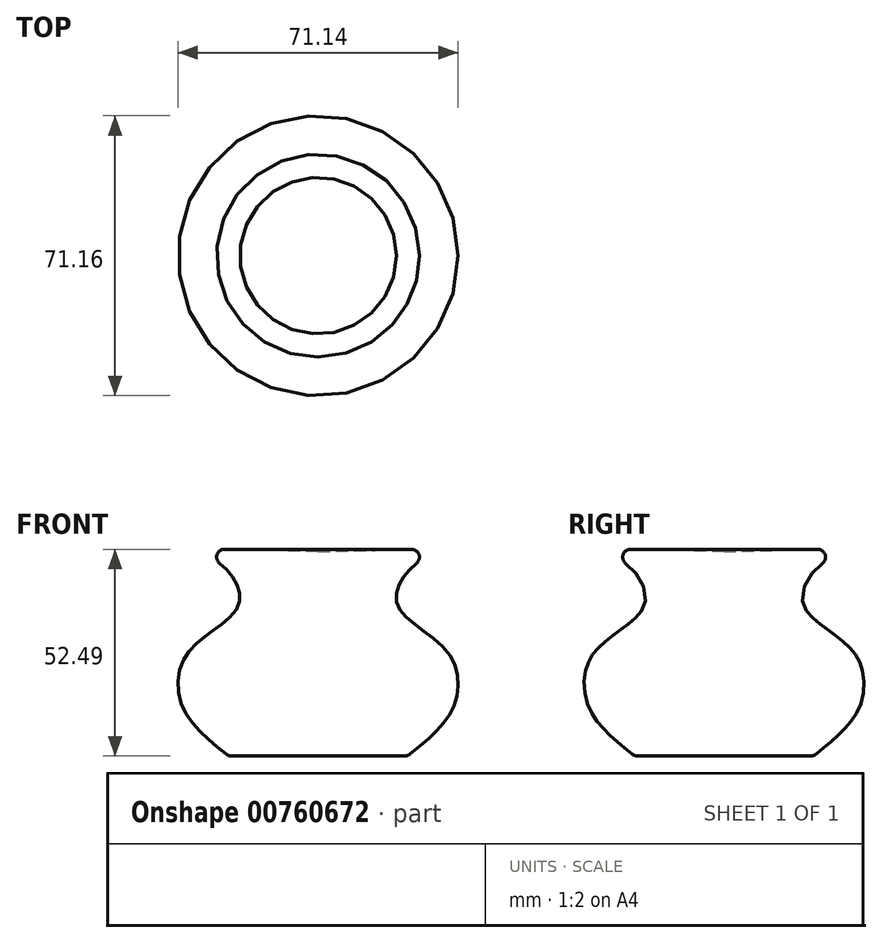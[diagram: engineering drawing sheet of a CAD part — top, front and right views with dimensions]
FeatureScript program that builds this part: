
annotation { "Feature Type Name" : "Feature", "Feature Type Description" : "" }
export const myFeature = defineFeature(function(context is Context, id is Id, definition is map)
    precondition{}
    {
        {
            var Q0;
            Q0=qCreatedBy(makeId("Front.planeOp"),FACE);
            var sketch = newSketch(context, id + "F0", { "sketchPlane" : qUnion([Q0])});
            skLineSegment(sketch, "E0", {"start": v(0, 0) * mm, "end": v(0, 72.8) * mm});
            skFitSpline(sketch, "E1", {"points": [v(32.64, 52.72) * mm, v(22.86, 46.9) * mm, v(20.48, 37.66) * mm, v(33.16, 26.03) * mm, v(34.22, 12.02) * mm, v(22.86, 0) * mm], "startDerivative": vector(-54.2, -13.95) * mm, "endDerivative": vector(-69.5, -58.85) * mm});
            skLineSegment(sketch, "E2", {"start": v(32.64, 52.72) * mm, "end": v(0, 51.87) * mm});
            skLineSegment(sketch, "E3", {"start": v(22.86, 0) * mm, "end": v(0, 0) * mm});
            skSolve(sketch);
        }
        {
            var Q0;
            Q0=sQuery(id+"F0.wireOp",EDGE,"E2");
            var Q1;
            Q1=sQuery(id+"F0.wireOp",EDGE,"E1");
            var Q2;
            Q2=sQuery(id+"F0.wireOp",EDGE,"E3");
            var Q3;
            Q3=sQuery(id+"F0.wireOp",EDGE,"E0");
            revolve(context, id + "F1", {"bodyType" : ToolBodyType.SURFACE, "surfaceOperationType" : NewSurfaceOperationType.NEW, "surfaceEntities" : qUnion([Q0, Q1, Q2]), "axis" : qUnion([Q3]), "revolveType" : RevolveType.FULL});
        }
        {
            var Q0;
            Q0=makeQuery(id+"F1.opRevolve","SWEPT_EDGE",EDGE,{"disambiguationData":[OSD([sQuery(id+"F0.wireOp",VERTEX,"E1.start")])]});
            var Q1;
            Q1=makeQuery(id+"F1.opRevolve","SWEPT_EDGE",EDGE,{"disambiguationData":[OSD([sQuery(id+"F0.wireOp",VERTEX,"E3.start")])]});
            fillet(context, id + "F2", {"entities" : qUnion([Q0, Q1]), "radius" : 2 * mm, "tangentPropagation" : true, "allowEdgeOverflow" : false});
        }
    });
